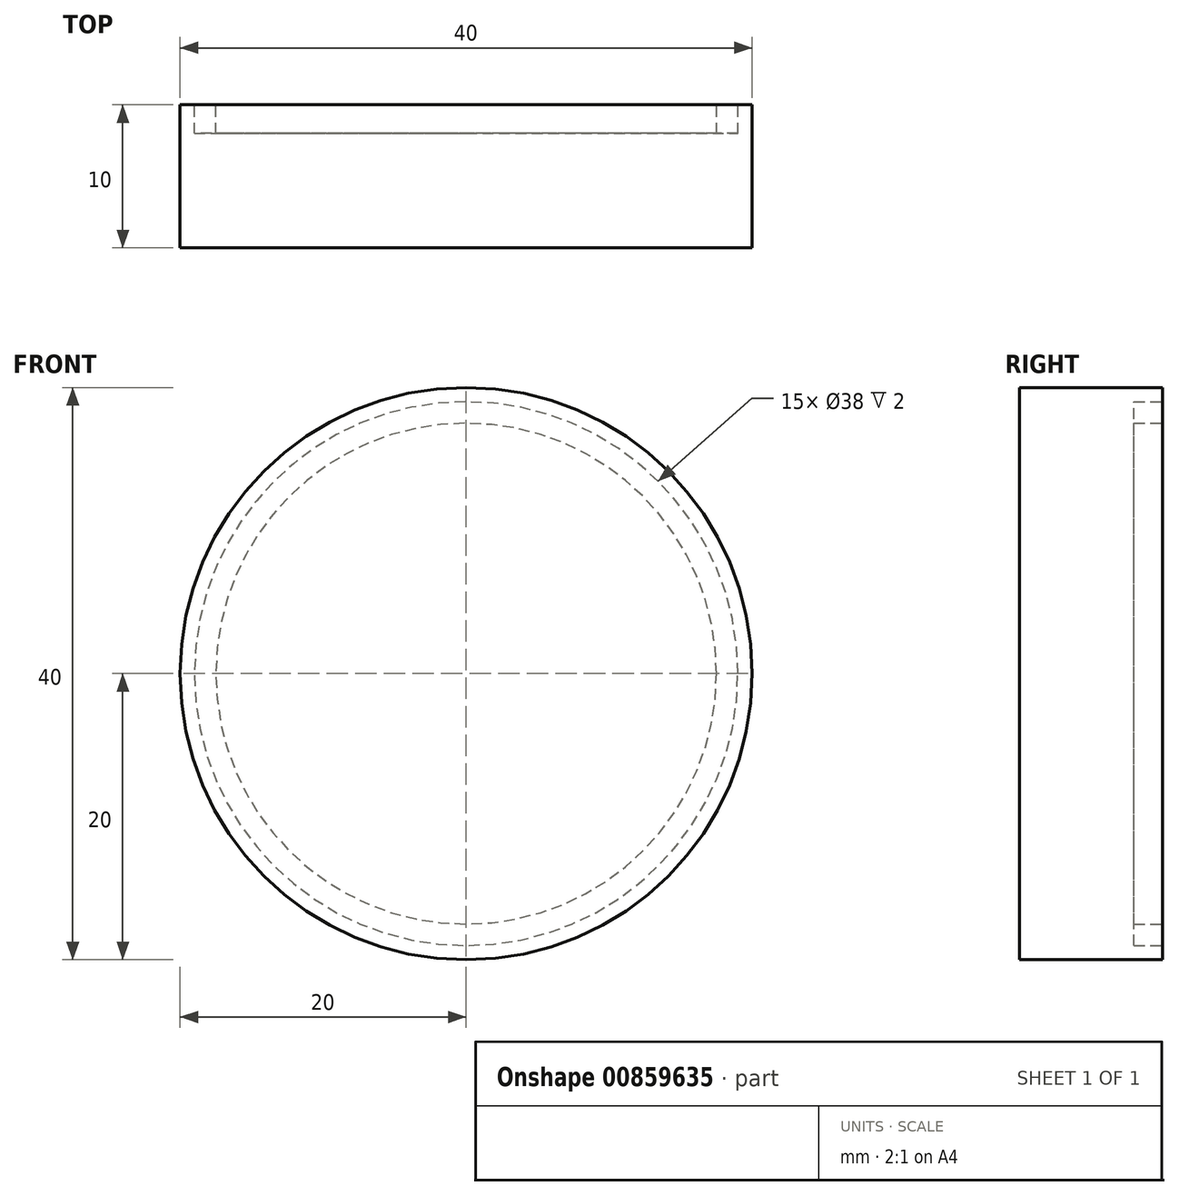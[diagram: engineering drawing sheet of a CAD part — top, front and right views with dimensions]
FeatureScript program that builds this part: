
annotation { "Feature Type Name" : "Feature", "Feature Type Description" : "" }
export const myFeature = defineFeature(function(context is Context, id is Id, definition is map)
    precondition{}
    {
        {
            var Q0;
            Q0=qCreatedBy(makeId("Front.planeOp"),FACE);
            var sketch = newSketch(context, id + "F0", { "sketchPlane" : qUnion([Q0])});
            skCircle(sketch, "E0", {"center": v(0, 0) * mm, "radius": 20 * mm});
            skSolve(sketch);
        }
        {
            var Q0;
            Q0 = qSketchRegion(id + "F0", true);
            extrude(context, id + "F1", {"entities" : qUnion([Q0]), "depth" : 10 * mm, "offsetDistance" : 25 * mm});
        }
        {
            var Q0;
            Q0=qCreatedBy(makeId("Front.planeOp"),FACE);
            var sketch = newSketch(context, id + "F2", { "sketchPlane" : qUnion([Q0])});
            skCircle(sketch, "E1", {"center": v(0, 0) * mm, "radius": 19 * mm});
            skCircle(sketch, "E2", {"center": v(0, 0) * mm, "radius": 17.5 * mm});
            skSolve(sketch);
        }
        {
            var Q0;
            Q0 = qSketchRegion(id + "F2", true);
            extrude(context, id + "F3", {"entities" : qUnion([Q0]), "operationType" : NewBodyOperationType.REMOVE, "depth" : 2 * mm, "offsetDistance" : 25 * mm});
        }
    });
